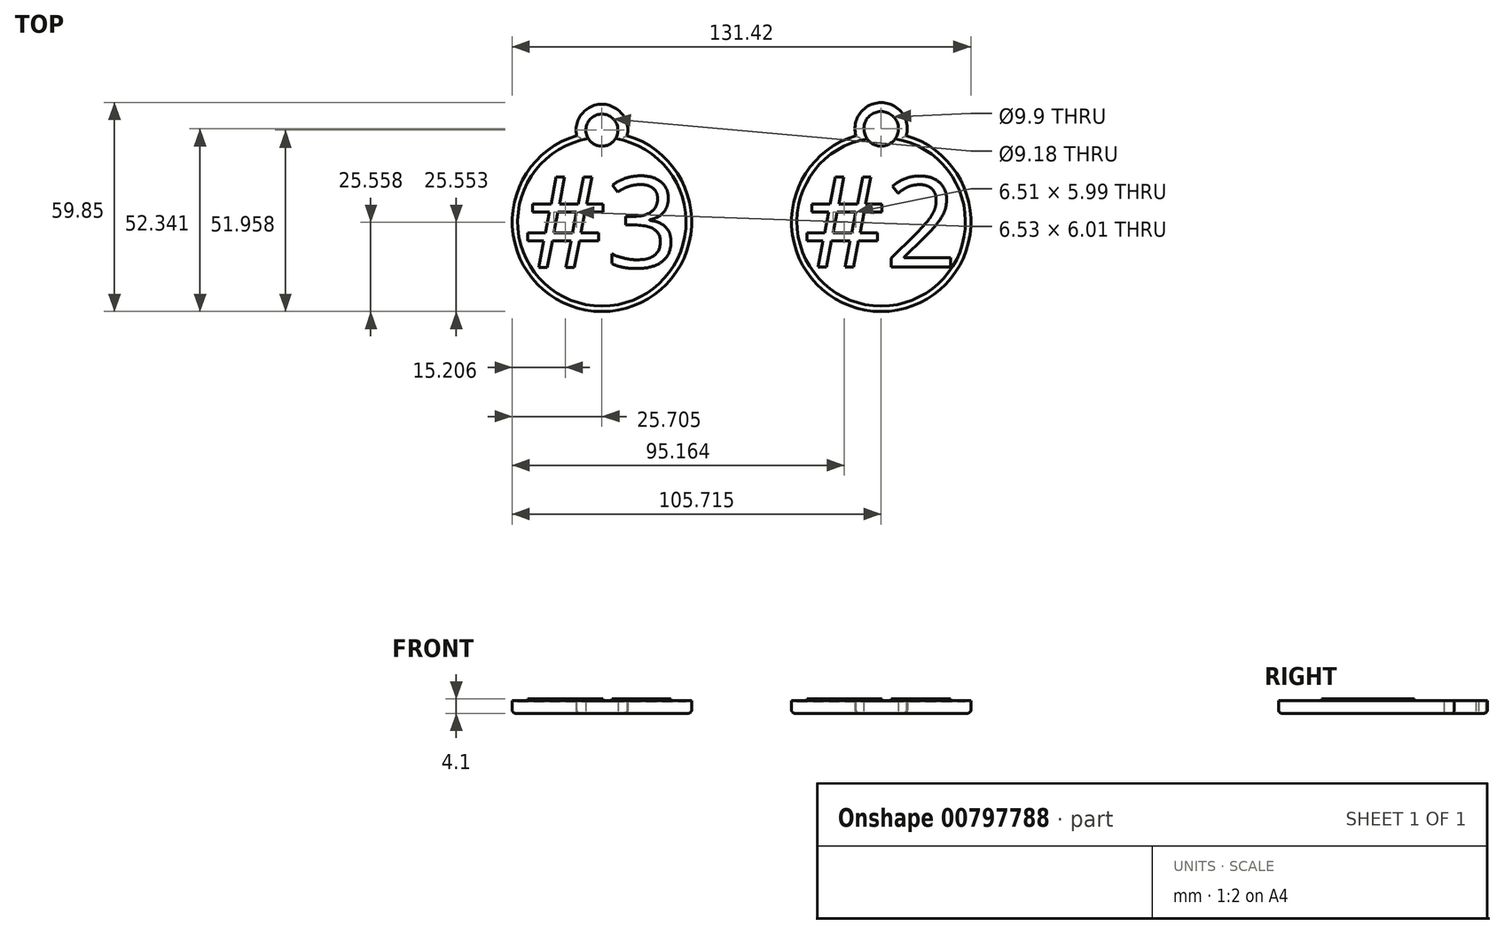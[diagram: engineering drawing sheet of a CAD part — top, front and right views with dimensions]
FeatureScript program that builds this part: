
annotation { "Feature Type Name" : "Feature", "Feature Type Description" : "" }
export const myFeature = defineFeature(function(context is Context, id is Id, definition is map)
    precondition{}
    {
        {
            var Q0;
            Q0=qCreatedBy(makeId("Top.planeOp"),FACE);
            var sketch = newSketch(context, id + "F0", { "sketchPlane" : qUnion([Q0])});
            skLineSegment(sketch, "E0", {"start": v(-47.24, 37.21) * mm, "end": v(-32.77, 37.21) * mm, "construction": true});
            skArc(sketch, "E1", {"start": v(-47.24, 37.21) * mm, "mid": v(-40, -13.15) * mm, "end": v(-32.77, 37.21) * mm});
            skArc(sketch, "E2.MirrorCS", {"start": v(47.24, 37.21) * mm, "mid": v(40, -13.15) * mm, "end": v(32.77, 37.21) * mm});
            skLineSegment(sketch, "E3", {"start": v(32.77, 37.21) * mm, "end": v(47.24, 37.21) * mm, "construction": true});
            skArc(sketch, "E4", {"start": v(-32.77, 37.21) * mm, "mid": v(-40, 46.22) * mm, "end": v(-47.24, 37.21) * mm});
            skArc(sketch, "E5", {"start": v(47.24, 37.21) * mm, "mid": v(40, 46.7) * mm, "end": v(32.77, 37.21) * mm});
            skCircle(sketch, "E6", {"center": v(-40, 38.8) * mm, "radius": 4.59 * mm});
            skCircle(sketch, "E7", {"center": v(40, 39.2) * mm, "radius": 4.95 * mm});
            skSolve(sketch);
        }
        {
            var Q0;
            Q0 = qSketchRegion(id + "F0", true);
            extrude(context, id + "F1", {"entities" : qUnion([Q0]), "depth" : 3.6 * mm, "offsetDistance" : 25.4 * mm});
        }
        {
            var Q0;
            Q0=makeQuery(id+"F1.opExtrude","CAP_EDGE",EDGE,{"disambiguationData":[OSD([sQuery(id+"F0.wireOp",EDGE,"E1")])],"isStart":true});
            var Q1;
            Q1=makeQuery(id+"F1.opExtrude","CAP_EDGE",EDGE,{"disambiguationData":[OSD([sQuery(id+"F0.wireOp",EDGE,"E2.MirrorCS")])],"isStart":true});
            var Q2;
            Q2=makeQuery(id+"F1.opExtrude","CAP_EDGE",EDGE,{"disambiguationData":[OSD([sQuery(id+"F0.wireOp",EDGE,"E4")])],"isStart":true});
            var Q3;
            Q3=makeQuery(id+"F1.opExtrude","CAP_EDGE",EDGE,{"disambiguationData":[OSD([sQuery(id+"F0.wireOp",EDGE,"E5")])],"isStart":true});
            fillet(context, id + "F2", {"entities" : qUnion([Q0, Q1, Q2, Q3]), "radius" : 1 * mm, "tangentPropagation" : true, "allowEdgeOverflow" : false});
        }
        {
            var Q0;
            Q0=makeQuery(id+"F1.opExtrude","CAP_FACE",FACE,{"disambiguationData":[OSD([sQuery(id+"F0.wireOp",EDGE,"E1"),sQuery(id+"F0.wireOp",EDGE,"E4"),sQuery(id+"F0.wireOp",EDGE,"E6")])],"isStart":false});
            var sketch = newSketch(context, id + "F3", { "sketchPlane" : qUnion([Q0])});
            skSolve(sketch);
        }
        {
            var Q0;
            Q0=makeQuery(id+"F3.imprint","IMPRINT",FACE,{"disambiguationData":[TD([[makeQuery(id+"F3.imprint","IMPRINT",EDGE,{"derivedFrom":makeQuery(id+"F1.opExtrude","CAP_EDGE",EDGE,{"disambiguationData":[OSD([sQuery(id+"F0.wireOp",EDGE,"E1")])],"isStart":false})}),1.0]])]});
            var sketch = newSketch(context, id + "F4", { "sketchPlane" : qUnion([Q0])});
            skCircle(sketch, "E8", {"center": v(-40, 12.55) * mm, "radius": 24.13 * mm});
            skCircle(sketch, "E9.MirrorC", {"center": v(40, 12.55) * mm, "radius": 24.13 * mm});
            skSolve(sketch);
        }
        {
            var Q0;
            Q0 = qSketchRegion(id + "F4", true);
            extrude(context, id + "F5", {"entities" : qUnion([Q0]), "operationType" : NewBodyOperationType.REMOVE, "oppositeDirection" : true, "depth" : 0.2 * mm, "offsetDistance" : 25 * mm});
        }
        {
            var Q0;
            Q0=makeQuery(id+"F3.imprint","IMPRINT",FACE,{"disambiguationData":[TD([[makeQuery(id+"F3.imprint","IMPRINT",EDGE,{"derivedFrom":makeQuery(id+"F1.opExtrude","CAP_EDGE",EDGE,{"disambiguationData":[OSD([sQuery(id+"F0.wireOp",EDGE,"E1")])],"isStart":false})}),1.0]])]});
            var sketch = newSketch(context, id + "F6", { "sketchPlane" : qUnion([Q0])});
            skCircle(sketch, "E10", {"center": v(-40, 12.55) * mm, "radius": 20 * mm, "construction": true});
            skCircle(sketch, "E11.MirrorC", {"center": v(40, 12.55) * mm, "radius": 20 * mm, "construction": true});
            skText(sketch, "E12", { "text": "#3", "fontName": "OpenSans-Regular.ttf"});
            skText(sketch, "E13", { "text": "#2", "fontName": "OpenSans-Regular.ttf"});
            const initialGuessF6  = {"E12": [-0.06216, -0.00048, 1, 0, 0.02606], "E13": [0.01783, -0.00044, 1, 0, 0.02599]};
            skSetInitialGuess(sketch, initialGuessF6);
            skSolve(sketch);
        }
        {
            var Q0;
            Q0 = qSketchRegion(id + "F6", true);
            extrude(context, id + "F7", {"entities" : qUnion([Q0]), "depth" : 0.5 * mm, "offsetDistance" : 25 * mm});
        }
    });
